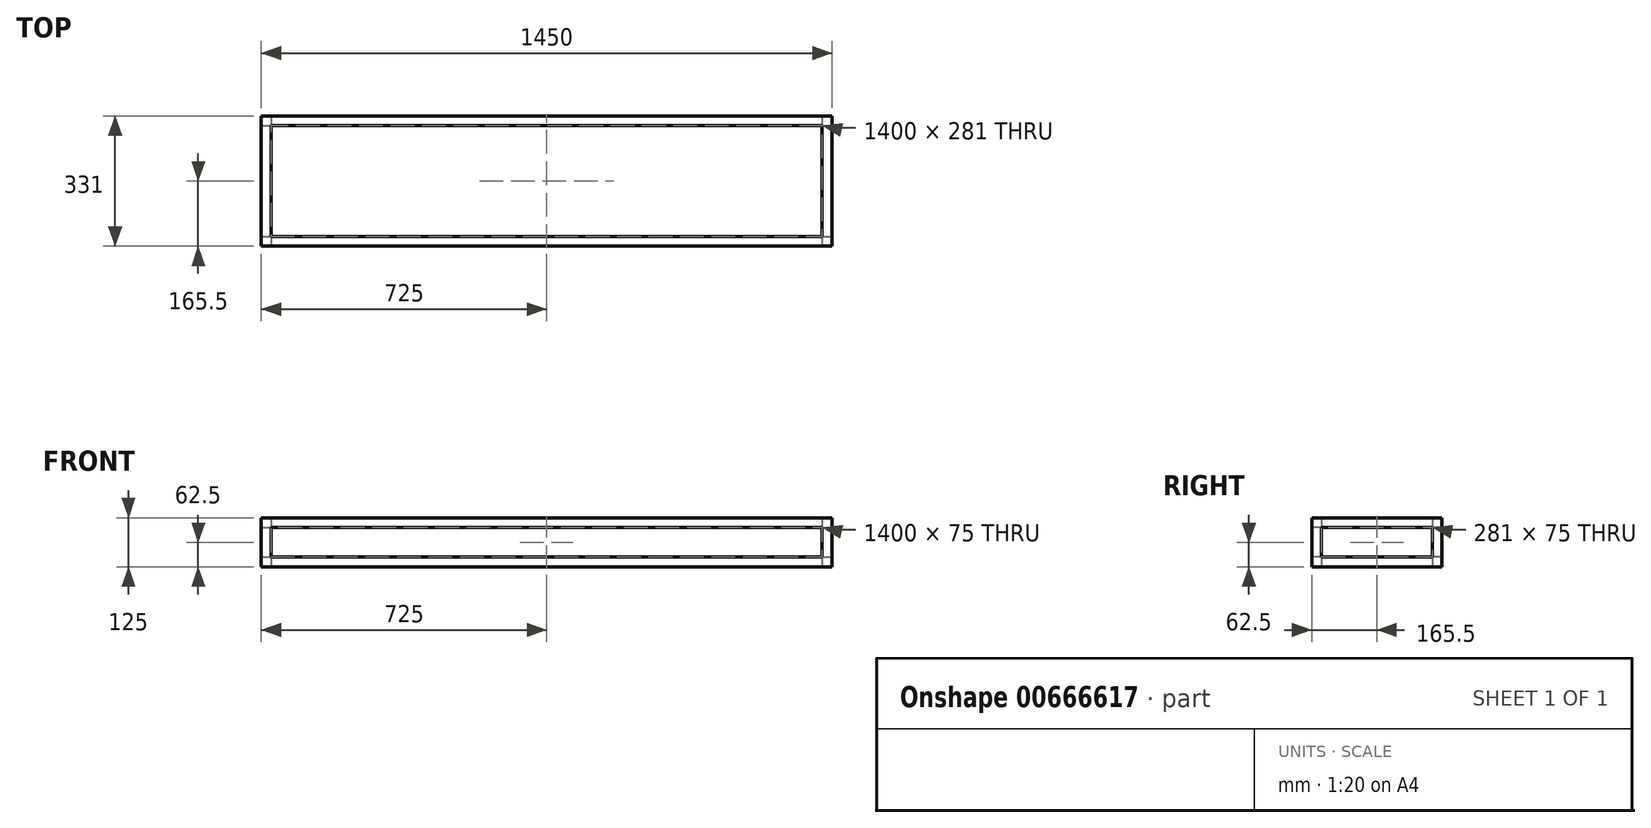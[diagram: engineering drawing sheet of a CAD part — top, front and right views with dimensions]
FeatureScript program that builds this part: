
annotation { "Feature Type Name" : "Feature", "Feature Type Description" : "" }
export const myFeature = defineFeature(function(context is Context, id is Id, definition is map)
    precondition{}
    {
        {
            var Q0;
            Q0=qCreatedBy(makeId("Front.planeOp"),FACE);
            var sketch = newSketch(context, id + "F0", { "sketchPlane" : qUnion([Q0])});
            skLineSegment(sketch, "E0.bottom", {"start": v(0, 0) * mm, "end": v(-1450, 0) * mm});
            skLineSegment(sketch, "E0.top", {"start": v(0, 125) * mm, "end": v(-1450, 125) * mm});
            skLineSegment(sketch, "E0.left", {"start": v(0, 0) * mm, "end": v(0, 125) * mm});
            skLineSegment(sketch, "E0.right", {"start": v(-1450, 0) * mm, "end": v(-1450, 125) * mm});
            skLineSegment(sketch, "E1.0", {"start": v(-25, 100) * mm, "end": v(-1425, 100) * mm});
            skLineSegment(sketch, "E1.1", {"start": v(-25, 25) * mm, "end": v(-25, 100) * mm});
            skLineSegment(sketch, "E1.2", {"start": v(-25, 25) * mm, "end": v(-1425, 25) * mm});
            skLineSegment(sketch, "E1.3", {"start": v(-1425, 25) * mm, "end": v(-1425, 100) * mm});
            skSolve(sketch);
        }
        {
            var Q0;
            Q0 = qSketchRegion(id + "F0", true);
            extrude(context, id + "F1", {"entities" : qUnion([Q0]), "oppositeDirection" : true, "depth" : 331 * mm, "offsetDistance" : 25 * mm});
        }
        {
            var Q0;
            Q0=qCreatedBy(makeId("Top.planeOp"),FACE);
            var sketch = newSketch(context, id + "F2", { "sketchPlane" : qUnion([Q0])});
            skLineSegment(sketch, "E2.0", {"start": v(-1425, 25) * mm, "end": v(-1425, 306) * mm});
            skLineSegment(sketch, "E2.1", {"start": v(-25, 25) * mm, "end": v(-1425, 25) * mm});
            skLineSegment(sketch, "E2.2", {"start": v(-25, 25) * mm, "end": v(-25, 306) * mm});
            skLineSegment(sketch, "E2.3", {"start": v(-25, 306) * mm, "end": v(-1425, 306) * mm});
            skSolve(sketch);
        }
        {
            var Q0;
            Q0 = qSketchRegion(id + "F2", true);
            extrude(context, id + "F3", {"entities" : qUnion([Q0]), "operationType" : NewBodyOperationType.REMOVE, "depth" : 377 * mm, "offsetDistance" : 25 * mm});
        }
        {
            var Q0;
            Q0=qCreatedBy(makeId("Right.planeOp"),FACE);
            var sketch = newSketch(context, id + "F4", { "sketchPlane" : qUnion([Q0])});
            skLineSegment(sketch, "E3.0", {"start": v(25, 100) * mm, "end": v(306, 100) * mm});
            skLineSegment(sketch, "E3.1", {"start": v(25, 25) * mm, "end": v(25, 100) * mm});
            skLineSegment(sketch, "E3.2", {"start": v(25, 25) * mm, "end": v(306, 25) * mm});
            skLineSegment(sketch, "E3.3", {"start": v(306, 25) * mm, "end": v(306, 100) * mm});
            skSolve(sketch);
        }
        {
            var Q0;
            Q0 = qSketchRegion(id + "F4", true);
            extrude(context, id + "F5", {"entities" : qUnion([Q0]), "operationType" : NewBodyOperationType.REMOVE, "oppositeDirection" : true, "depth" : 1538 * mm, "offsetDistance" : 25 * mm});
        }
    });
